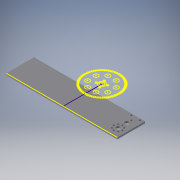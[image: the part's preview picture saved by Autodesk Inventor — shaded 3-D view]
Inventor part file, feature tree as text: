
AUTODESK INVENTOR PART (.ipt)
format: ipt  version: 2016 (Build 200138000, 138)  size: 251,904 bytes
history: native  units: in
note: dims shown in document units (in); Inventor stores cm internally (conversion verified against a paired STEP export)
features: sketch x4, reference x4, extrude x3
ambient origin geometry x8: Origin, YZ Plane, XZ Plane, XY Plane, X Axis, Y Axis, Z Axis, Center Point
bodies: Solid1 (feature_tree)
feature tree (11):
  extrude  "Extrusion1"  Depth=8.0in
  extrude  "Extrusion2"  Depth=0.13in TaperAngle=0.0deg
  sketch  "Sketch3"  dims[d6=0.5625in d7=0.0in]
  extrude  "Extrusion3"  [1 undecoded]
  sketch  "Sketch1"  dims[d0=2.0in d1=8.0in]
  sketch  "Sketch2"  dims[d2=0.13in d3=0.0in d4=0.8075in d5=0.0in]
  reference  "Reference1"
  reference  "Reference2"
  reference  "Reference3"
  sketch  "Sketch4"
  reference  "Reference4"
note: 1 required parameter value undecoded (feature->parameter linkage not recoverable at this tier; creation-order binding heuristic only, values carry confidence <= 0.55)
